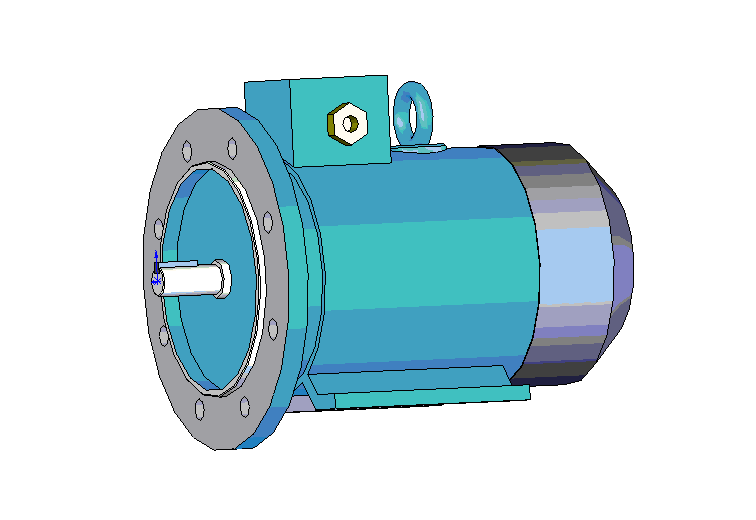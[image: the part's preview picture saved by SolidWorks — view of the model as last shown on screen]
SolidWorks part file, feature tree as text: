
SOLIDWORKS PART (.sldprt)
format: sldprt  version: not decoded by parser v0  size: 753,664 bytes
history: native  units: mm
features: sketch x18, extrude x13, plane x4, chamfer x3, cut_extrude x3, material x1, sweep x1 (+10 scaffold rows collapsed)
feature tree (53):
  scaffold x10  (default folders/planes/origin — collapsed)
  material  "Ст.3 ГОСТ 380-88"
  plane  "Спереди"
  plane  "Сверху"
  plane  "Справа"
  sketch  "Эскиз1"  dims[D1=14.0mm]
  extrude  "Вытянуть1"  Depth=30mm
  sketch  "Эскиз2"  dims[D1=5.0mm D2=5.0mm D3=16.0mm]
  extrude  "Вытянуть2"  Depth=20mm
  sketch  "Эскиз3"  dims[D1=18.0mm]
  extrude  "Вытянуть3"  Depth=4mm
  sketch  "Эскиз4"  dims[D1=160.0mm D2=104.0mm]
  extrude  "Вытянуть4"  Depth=10mm
  sketch  "Эскиз5"  dims[D1=106.0mm]
  extrude  "Вытянуть5"  Depth=26mm
  sketch  "Эскиз7"  dims[D1=110.0mm D2=104.0mm]
  extrude  "Вытянуть6"  Depth=7.5mm
  chamfer  "Фаска1"  Distance=0.5mm Angle=45deg
  sketch  "Эскиз8"  dims[c1.D2=10.0mm c1.D1=~97.363905mm c2.D1=22.5deg c2.D3=65.0mm c2.D4=65.0mm c2.D5=65.0mm]
  cut_extrude  "Вырез-Вытянуть1"  [1 undecoded]
  sketch  "Эскиз10"  dims[D1=112.0mm]
  extrude  "Вытянуть7"  Depth=110mm
  sketch  "Эскиз11"  dims[D1=113.0mm]
  extrude  "Вытянуть8"  Depth=57mm
  chamfer  "Фаска2"  Distance=19mm Angle=45deg
  sketch  "Эскиз12"  dims[c1.D1=120.0mm c1.D2=63.0mm c1.D3=7.0mm c1.D4=7.0mm c1.D5=~25.141734mm c2.D5=~179.215467deg c3.D5=7.0mm c3.D6=~26.415369mm c4.D6=45.0deg c4.D7=~25.141734mm c5.D7=45.0deg]
  extrude  "Вытянуть9"  Depth=100mm
  sketch  "Эскиз13"  dims[c1.D2=7.0mm c1.D5=7.0mm c1.D7=7.0mm c1.D8=7.0mm c1.D9=7.0mm c1.D10=7.0mm c1.D1=70.0mm c2.D2=~10.820423mm c2.D3=50.0mm c2.D4=90.0deg c2.D5=80.0mm c2.D6=100.0mm c2.D9=~11.783562mm c3.D9=100.0mm c3.D10=80.0mm c3.D11=150.0mm]
  cut_extrude  "Вырез-Вытянуть2"  [1 undecoded]
  sketch  "Эскиз14"  dims[D1=50.0mm D2=50.0mm D3=1.0mm]
  extrude  "Вытянуть10"  Depth=91mm
  sketch  "Эскиз15"  dims[D1=30.0mm D2=135.0mm]
  extrude  "Вытянуть11"  Depth=58mm
  chamfer  "Фаска3"  Distance=1mm Angle=45deg
  plane  "Плоскость1"  Offset=135mm
  sketch  "Эскиз16"  dims[D1=26.0mm]
  sketch  "Эскиз17"  dims[D1=8.0mm D2=26.0mm]
  sweep  "По траектории1"
  sketch  "Эскиз18"  dims[D1=14.0mm D2=25.0mm D3=22.0mm]
  extrude  "Вытянуть12"  Depth=4mm
  sketch  "Эскиз19"  dims[D1=~1.314955mm]
  extrude  "Вытянуть13"  Depth=7mm
  sketch  "Эскиз20"  dims[D1=8.0mm]
  cut_extrude  "Вырез-Вытянуть3"  Depth=7mm
decode coverage: 35 of 38 modeling features carry decoded parameters
note: ~ marks probable driven/reference dimensions
note: 2 parameter values undecoded
note: suppression state not decoded; provenance and decode notes live in map.json
